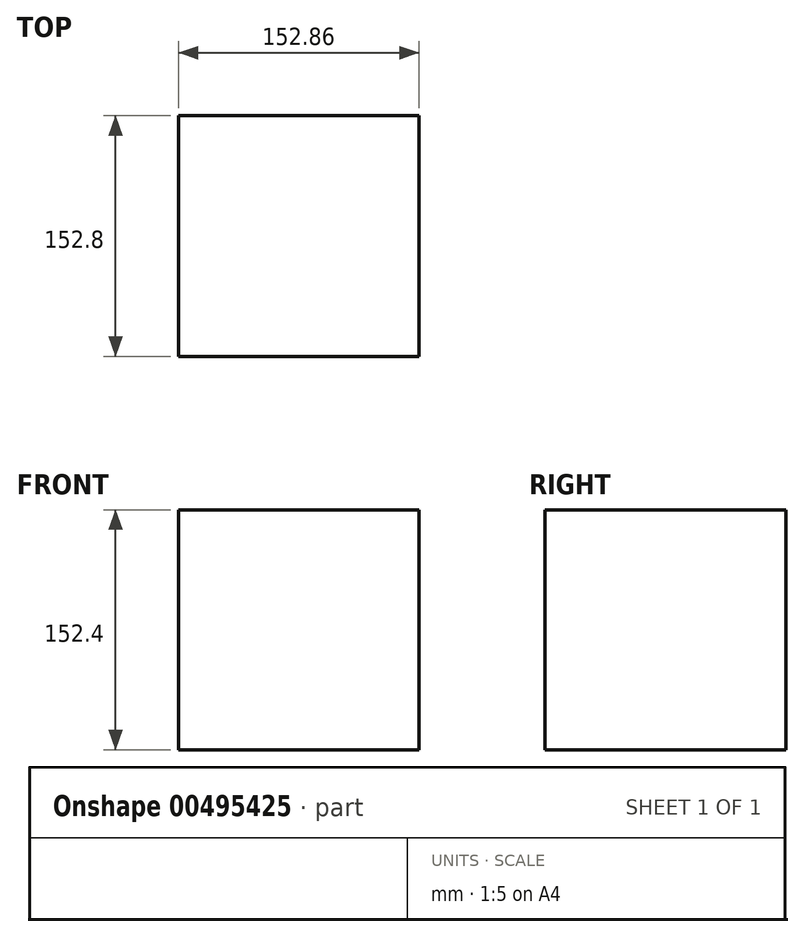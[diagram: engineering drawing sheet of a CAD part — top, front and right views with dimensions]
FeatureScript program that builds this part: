
annotation { "Feature Type Name" : "Feature", "Feature Type Description" : "" }
export const myFeature = defineFeature(function(context is Context, id is Id, definition is map)
    precondition{}
    {
        {
            var Q0;
            Q0=qCreatedBy(makeId("Top.planeOp"),FACE);
            var sketch = newSketch(context, id + "F0", { "sketchPlane" : qUnion([Q0])});
            skLineSegment(sketch, "E0.bottom", {"start": v(-76.43, 76.4) * mm, "end": v(76.43, 76.4) * mm});
            skLineSegment(sketch, "E0.top", {"start": v(-76.43, -76.4) * mm, "end": v(76.43, -76.4) * mm});
            skLineSegment(sketch, "E0.left", {"start": v(-76.43, 76.4) * mm, "end": v(-76.43, -76.4) * mm});
            skLineSegment(sketch, "E0.right", {"start": v(76.43, 76.4) * mm, "end": v(76.43, -76.4) * mm});
            skPoint(sketch, "E0.middle", {"position": v(0, 0) * mm});
            skSolve(sketch);
        }
        {
            var Q0;
            Q0 = qSketchRegion(id + "F0", true);
            extrude(context, id + "F1", {"entities" : qUnion([Q0]), "endBound" : BoundingType.SYMMETRIC, "depth" : 152.4 * mm});
        }
    });
